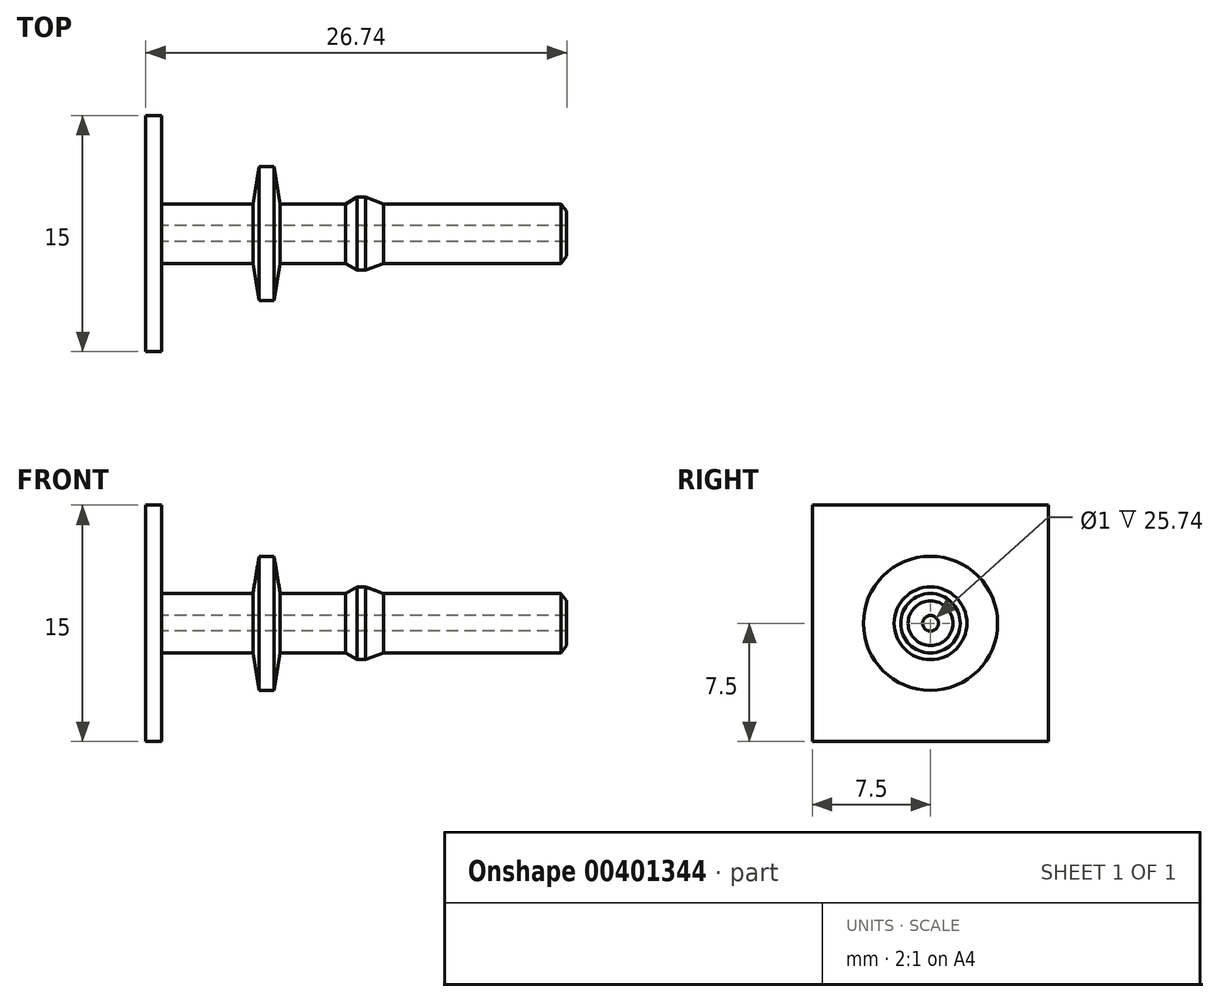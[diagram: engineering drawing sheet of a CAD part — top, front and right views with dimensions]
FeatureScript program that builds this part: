
annotation { "Feature Type Name" : "Feature", "Feature Type Description" : "" }
export const myFeature = defineFeature(function(context is Context, id is Id, definition is map)
    precondition{}
    {
        {
            var Q0;
            Q0=qCreatedBy(makeId("Front.planeOp"),FACE);
            var sketch = newSketch(context, id + "F0", { "sketchPlane" : qUnion([Q0])});
            skLineSegment(sketch, "E0", {"start": v(-5.12, 0.5) * mm, "end": v(20.62, 0.5) * mm});
            skLineSegment(sketch, "E1", {"start": v(20.62, 0.5) * mm, "end": v(20.62, 1.42) * mm});
            skLineSegment(sketch, "E2", {"start": v(20.62, 1.42) * mm, "end": v(20.25, 1.9) * mm});
            skLineSegment(sketch, "E3", {"start": v(20.25, 1.9) * mm, "end": v(8.97, 1.9) * mm});
            skLineSegment(sketch, "E4", {"start": v(8.97, 1.9) * mm, "end": v(7.84, 2.31) * mm});
            skLineSegment(sketch, "E5", {"start": v(7.84, 2.31) * mm, "end": v(7.29, 2.31) * mm});
            skLineSegment(sketch, "E6", {"start": v(7.29, 2.31) * mm, "end": v(6.58, 1.89) * mm});
            skLineSegment(sketch, "E7", {"start": v(6.58, 1.89) * mm, "end": v(2.42, 1.89) * mm});
            skLineSegment(sketch, "E8", {"start": v(2.42, 1.89) * mm, "end": v(2.02, 4.26) * mm});
            skLineSegment(sketch, "E9", {"start": v(0, 1.89) * mm, "end": v(-5.12, 1.89) * mm});
            skLineSegment(sketch, "E10", {"start": v(-5.12, 1.89) * mm, "end": v(-5.12, 0.5) * mm});
            skLineSegment(sketch, "E11", {"start": v(2.02, 4.26) * mm, "end": v(1.08, 4.26) * mm});
            skLineSegment(sketch, "E12", {"start": v(1.08, 4.26) * mm, "end": v(0.69, 1.89) * mm});
            skLineSegment(sketch, "E13", {"start": v(0.69, 1.89) * mm, "end": v(0, 1.89) * mm});
            skLineSegment(sketch, "E14", {"start": v(-6.85, 0) * mm, "end": v(25.14, 0) * mm});
            skSolve(sketch);
        }
        {
            var Q0;
            Q0=qSketchRegion(id+"F0",true);
            var Q1;
            Q1=sQuery(id+"F0.wireOp",EDGE,"E14");
            revolve(context, id + "F1", {"entities" : qUnion([Q0]), "axis" : qUnion([Q1]), "revolveType" : RevolveType.FULL});
        }
        {
            var Q0;
            Q0=makeQuery(id+"F1.opRevolve","SWEPT_FACE",FACE,{"disambiguationData":[OSD([sQuery(id+"F0.wireOp",EDGE,"E10")])]});
            var sketch = newSketch(context, id + "F2", { "sketchPlane" : qUnion([Q0])});
            skLineSegment(sketch, "E15.bottom", {"start": v(-7.5, -7.5) * mm, "end": v(7.5, -7.5) * mm});
            skLineSegment(sketch, "E15.top", {"start": v(-7.5, 7.5) * mm, "end": v(7.5, 7.5) * mm});
            skLineSegment(sketch, "E15.left", {"start": v(-7.5, -7.5) * mm, "end": v(-7.5, 7.5) * mm});
            skLineSegment(sketch, "E15.right", {"start": v(7.5, -7.5) * mm, "end": v(7.5, 7.5) * mm});
            skPoint(sketch, "E15.middle", {"position": v(0, 0) * mm});
            skSolve(sketch);
        }
        {
            var Q0;
            Q0=qSketchRegion(id+"F2",true);
            extrude(context, id + "F3", {"entities" : qUnion([Q0]), "operationType" : NewBodyOperationType.ADD, "depth" : 1 * mm});
        }
    });
